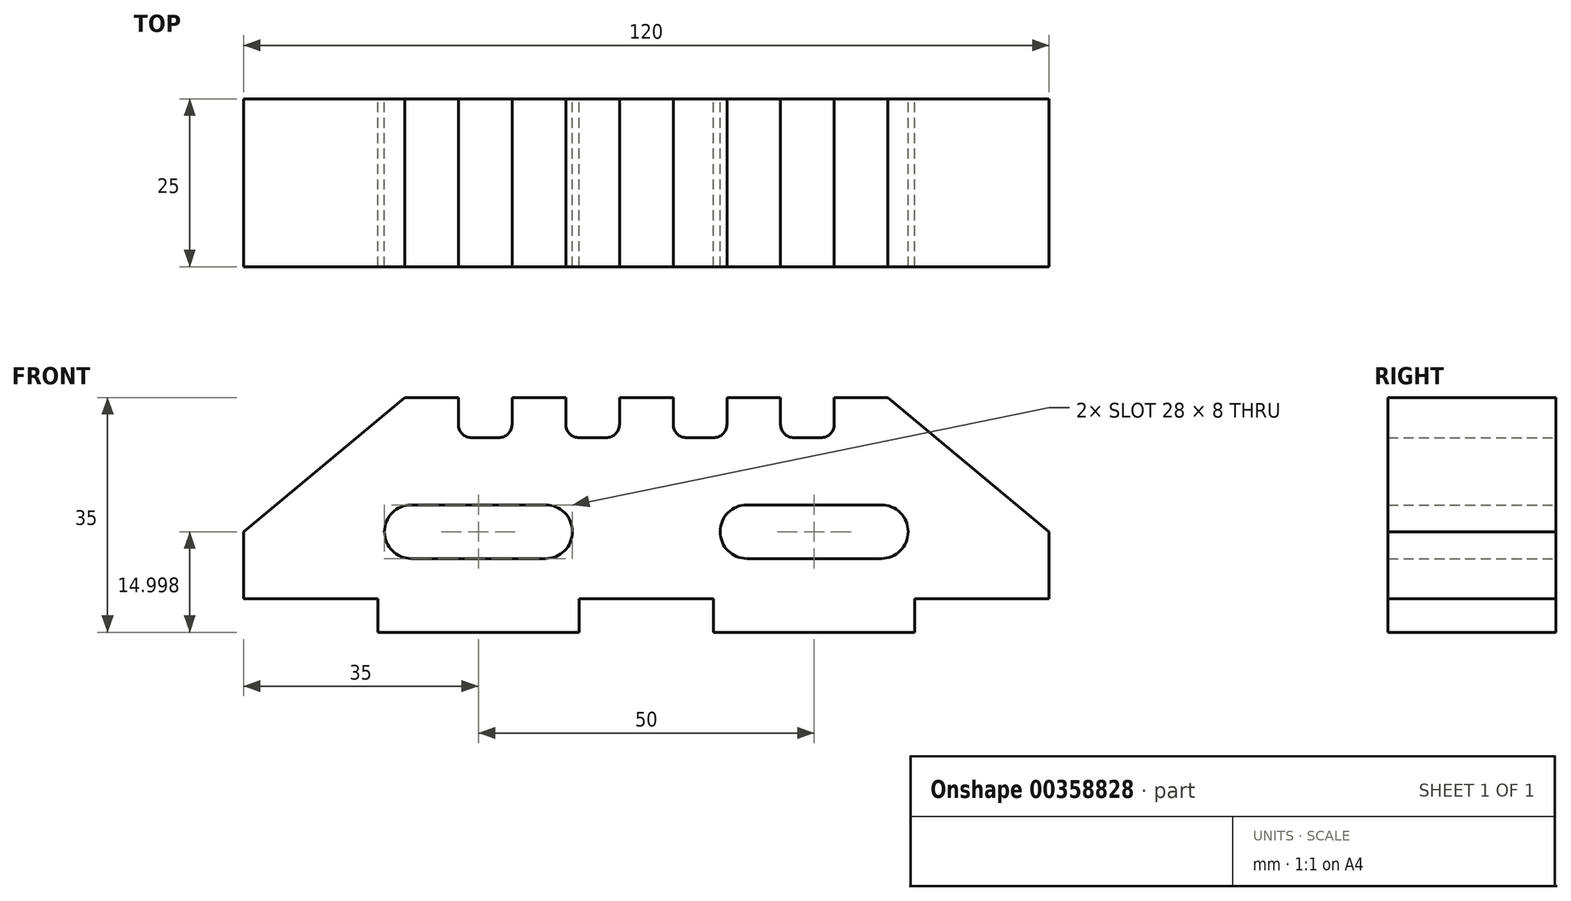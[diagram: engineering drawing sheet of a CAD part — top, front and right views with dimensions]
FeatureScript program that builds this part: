
annotation { "Feature Type Name" : "Feature", "Feature Type Description" : "" }
export const myFeature = defineFeature(function(context is Context, id is Id, definition is map)
    precondition{}
    {
        {
            var Q0;
            Q0=qCreatedBy(makeId("Front.planeOp"),FACE);
            var sketch = newSketch(context, id + "F0", { "sketchPlane" : qUnion([Q0])});
            skLineSegment(sketch, "E0", {"start": v(-18.23, -18.5) * mm, "end": v(1.77, -18.5) * mm});
            skLineSegment(sketch, "E1", {"start": v(1.77, -18.5) * mm, "end": v(1.77, -23.5) * mm});
            skLineSegment(sketch, "E2", {"start": v(-18.23, -18.5) * mm, "end": v(-18.23, -23.5) * mm});
            skLineSegment(sketch, "E3", {"start": v(1.77, -23.5) * mm, "end": v(31.77, -23.5) * mm});
            skLineSegment(sketch, "E4", {"start": v(31.77, -23.5) * mm, "end": v(31.77, -18.5) * mm});
            skLineSegment(sketch, "E5", {"start": v(31.77, -18.5) * mm, "end": v(51.77, -18.5) * mm});
            skLineSegment(sketch, "E6", {"start": v(-18.23, -23.5) * mm, "end": v(-48.23, -23.5) * mm});
            skLineSegment(sketch, "E7", {"start": v(-48.23, -23.5) * mm, "end": v(-48.23, -18.5) * mm});
            skLineSegment(sketch, "E8", {"start": v(-48.23, -18.5) * mm, "end": v(-68.23, -18.5) * mm});
            skLineSegment(sketch, "E9", {"start": v(-68.23, -18.5) * mm, "end": v(-68.23, -8.5) * mm});
            skLineSegment(sketch, "E10", {"start": v(51.77, -18.5) * mm, "end": v(51.77, -8.5) * mm});
            skLineSegment(sketch, "E11", {"start": v(-44.23, 11.5) * mm, "end": v(-68.23, -8.5) * mm});
            skLineSegment(sketch, "E12", {"start": v(-44.23, 11.5) * mm, "end": v(-36.23, 11.5) * mm});
            skLineSegment(sketch, "E13", {"start": v(-36.23, 11.5) * mm, "end": v(-36.23, 7.5) * mm});
            skLineSegment(sketch, "E14", {"start": v(-34.23, 5.5) * mm, "end": v(-30.23, 5.5) * mm});
            skLineSegment(sketch, "E15", {"start": v(-28.23, 7.5) * mm, "end": v(-28.23, 11.5) * mm});
            skLineSegment(sketch, "E16", {"start": v(-28.23, 11.5) * mm, "end": v(-20.23, 11.5) * mm});
            skLineSegment(sketch, "E17", {"start": v(-20.23, 11.5) * mm, "end": v(-20.23, 7.5) * mm});
            skLineSegment(sketch, "E18", {"start": v(-18.23, 5.5) * mm, "end": v(-14.23, 5.5) * mm});
            skLineSegment(sketch, "E19", {"start": v(-12.23, 7.5) * mm, "end": v(-12.23, 11.5) * mm});
            skLineSegment(sketch, "E20", {"start": v(-12.23, 11.5) * mm, "end": v(-4.23, 11.5) * mm});
            skLineSegment(sketch, "E21", {"start": v(-4.23, 11.5) * mm, "end": v(-4.23, 7.5) * mm});
            skLineSegment(sketch, "E22", {"start": v(-2.23, 5.5) * mm, "end": v(1.77, 5.5) * mm});
            skLineSegment(sketch, "E23", {"start": v(3.77, 7.5) * mm, "end": v(3.77, 11.5) * mm});
            skLineSegment(sketch, "E24", {"start": v(3.77, 11.5) * mm, "end": v(11.77, 11.5) * mm});
            skLineSegment(sketch, "E25", {"start": v(11.77, 11.5) * mm, "end": v(11.77, 7.5) * mm});
            skLineSegment(sketch, "E26", {"start": v(13.77, 5.5) * mm, "end": v(17.77, 5.5) * mm});
            skLineSegment(sketch, "E27", {"start": v(19.77, 7.5) * mm, "end": v(19.77, 11.5) * mm});
            skLineSegment(sketch, "E28", {"start": v(19.77, 11.5) * mm, "end": v(27.77, 11.5) * mm});
            skLineSegment(sketch, "E29", {"start": v(27.77, 11.5) * mm, "end": v(51.77, -8.5) * mm});
            skLineSegment(sketch, "E30", {"start": v(6.77, -12.5) * mm, "end": v(26.77, -12.5) * mm});
            skLineSegment(sketch, "E31", {"start": v(30.77, -8.5) * mm, "end": v(30.77, -8.5) * mm});
            skLineSegment(sketch, "E32", {"start": v(26.77, -4.5) * mm, "end": v(6.77, -4.5) * mm});
            skLineSegment(sketch, "E33", {"start": v(2.77, -8.5) * mm, "end": v(2.77, -8.5) * mm});
            skPoint(sketch, "E34.visualSharp", {"position": v(2.77, -12.5) * mm});
            skArc(sketch, "E34.filletArc", {"start": v(2.77, -8.5) * mm, "mid": v(3.94, -11.32) * mm, "end": v(6.77, -12.5) * mm});
            skPoint(sketch, "E35.visualSharp", {"position": v(2.77, -4.5) * mm});
            skArc(sketch, "E35.filletArc", {"start": v(6.77, -4.5) * mm, "mid": v(3.94, -5.66) * mm, "end": v(2.77, -8.5) * mm});
            skPoint(sketch, "E36.visualSharp", {"position": v(30.77, -4.5) * mm});
            skArc(sketch, "E36.filletArc", {"start": v(30.77, -8.5) * mm, "mid": v(29.6, -5.66) * mm, "end": v(26.77, -4.5) * mm});
            skPoint(sketch, "E37.visualSharp", {"position": v(30.77, -12.5) * mm});
            skArc(sketch, "E37.filletArc", {"start": v(26.77, -12.5) * mm, "mid": v(29.6, -11.32) * mm, "end": v(30.77, -8.5) * mm});
            skLineSegment(sketch, "E38", {"start": v(-23.23, -12.5) * mm, "end": v(-43.23, -12.5) * mm});
            skLineSegment(sketch, "E39", {"start": v(-47.23, -8.5) * mm, "end": v(-47.23, -8.5) * mm});
            skLineSegment(sketch, "E40", {"start": v(-43.23, -4.5) * mm, "end": v(-23.23, -4.5) * mm});
            skLineSegment(sketch, "E41", {"start": v(-19.23, -8.5) * mm, "end": v(-19.23, -8.5) * mm});
            skPoint(sketch, "E42.end.orphan", {"position": v(-18.23, -12.5) * mm});
            skPoint(sketch, "E43.visualSharp", {"position": v(-19.23, -12.5) * mm});
            skArc(sketch, "E43.filletArc", {"start": v(-23.23, -12.5) * mm, "mid": v(-20.4, -11.32) * mm, "end": v(-19.23, -8.5) * mm});
            skPoint(sketch, "E44.visualSharp", {"position": v(-19.23, -4.5) * mm});
            skArc(sketch, "E44.filletArc", {"start": v(-19.23, -8.5) * mm, "mid": v(-20.4, -5.66) * mm, "end": v(-23.23, -4.5) * mm});
            skPoint(sketch, "E45.visualSharp", {"position": v(-47.23, -4.5) * mm});
            skArc(sketch, "E45.filletArc", {"start": v(-43.23, -4.5) * mm, "mid": v(-46.06, -5.66) * mm, "end": v(-47.23, -8.5) * mm});
            skPoint(sketch, "E46.visualSharp", {"position": v(-47.23, -12.5) * mm});
            skArc(sketch, "E46.filletArc", {"start": v(-47.23, -8.5) * mm, "mid": v(-46.06, -11.32) * mm, "end": v(-43.23, -12.5) * mm});
            skPoint(sketch, "E47.visualSharp", {"position": v(-36.23, 5.5) * mm});
            skArc(sketch, "E47.filletArc", {"start": v(-36.23, 7.5) * mm, "mid": v(-35.64, 6.1) * mm, "end": v(-34.23, 5.5) * mm});
            skPoint(sketch, "E48.visualSharp", {"position": v(-28.23, 5.5) * mm});
            skArc(sketch, "E48.filletArc", {"start": v(-30.23, 5.5) * mm, "mid": v(-28.82, 6.1) * mm, "end": v(-28.23, 7.5) * mm});
            skPoint(sketch, "E49.visualSharp", {"position": v(-20.23, 5.5) * mm});
            skArc(sketch, "E49.filletArc", {"start": v(-20.23, 7.5) * mm, "mid": v(-19.64, 6.1) * mm, "end": v(-18.23, 5.5) * mm});
            skPoint(sketch, "E50.visualSharp", {"position": v(-12.23, 5.5) * mm});
            skArc(sketch, "E50.filletArc", {"start": v(-14.23, 5.5) * mm, "mid": v(-12.82, 6.1) * mm, "end": v(-12.23, 7.5) * mm});
            skPoint(sketch, "E51.visualSharp", {"position": v(-4.23, 5.5) * mm});
            skArc(sketch, "E51.filletArc", {"start": v(-4.23, 7.5) * mm, "mid": v(-3.64, 6.1) * mm, "end": v(-2.23, 5.5) * mm});
            skPoint(sketch, "E52.visualSharp", {"position": v(3.77, 5.5) * mm});
            skArc(sketch, "E52.filletArc", {"start": v(1.77, 5.5) * mm, "mid": v(3.18, 6.1) * mm, "end": v(3.77, 7.5) * mm});
            skPoint(sketch, "E53.visualSharp", {"position": v(11.77, 5.5) * mm});
            skArc(sketch, "E53.filletArc", {"start": v(11.77, 7.5) * mm, "mid": v(12.36, 6.1) * mm, "end": v(13.77, 5.5) * mm});
            skPoint(sketch, "E54.visualSharp", {"position": v(19.77, 5.5) * mm});
            skArc(sketch, "E54.filletArc", {"start": v(17.77, 5.5) * mm, "mid": v(19.18, 6.1) * mm, "end": v(19.77, 7.5) * mm});
            skSolve(sketch);
        }
        {
            var Q0;
            Q0=makeQuery(id+"F0.imprint","IMPRINT",FACE,{"disambiguationData":[TD([[makeQuery(id+"F0.imprint","IMPRINT",EDGE,{"derivedFrom":sQuery(id+"F0.wireOp",EDGE,"E0")}),1.0]])]});
            extrude(context, id + "F1", {"entities" : qUnion([Q0]), "depth" : 25 * mm});
        }
    });
